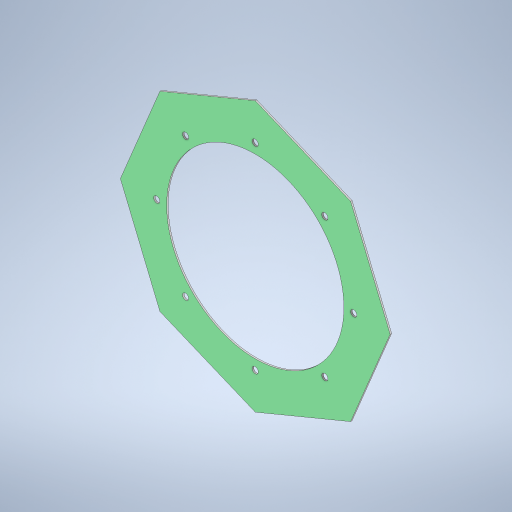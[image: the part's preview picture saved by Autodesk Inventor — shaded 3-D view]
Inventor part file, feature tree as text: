
AUTODESK INVENTOR PART (.ipt)
format: ipt  version: 2024.2 (Build 282272000, 272)  size: 305,664 bytes
history: native  units: mm
features: sketch x2, other x2, sheet_metal_op x1, extrude x1, pattern_circular x1
ambient origin geometry x8: Origin, YZ Plane, XZ Plane, XY Plane, X Axis, Y Axis, Z Axis, Center Point
bodies: Solid1 (feature_tree)
feature tree (7):
  sheet_metal_op  "Face1"
  extrude  "Extrusion1"  Depth=200.0mm
  pattern_circular  "Circular Pattern1"  Count=20  [1 undecoded]
  sketch  "Sketch2"  dims[d15=3.0mm d16=12.5mm d17=200.0mm]
  other  "Plate1"
  sketch  "Sketch4"  dims[d18=10.0mm d19=0.0mm d20=80.0mm d21=360.0deg d23=506.0mm d26=360.0mm]
  other  "Definition1"
note: 1 required parameter value undecoded (feature->parameter linkage not recoverable at this tier; creation-order binding heuristic only, values carry confidence <= 0.55)
